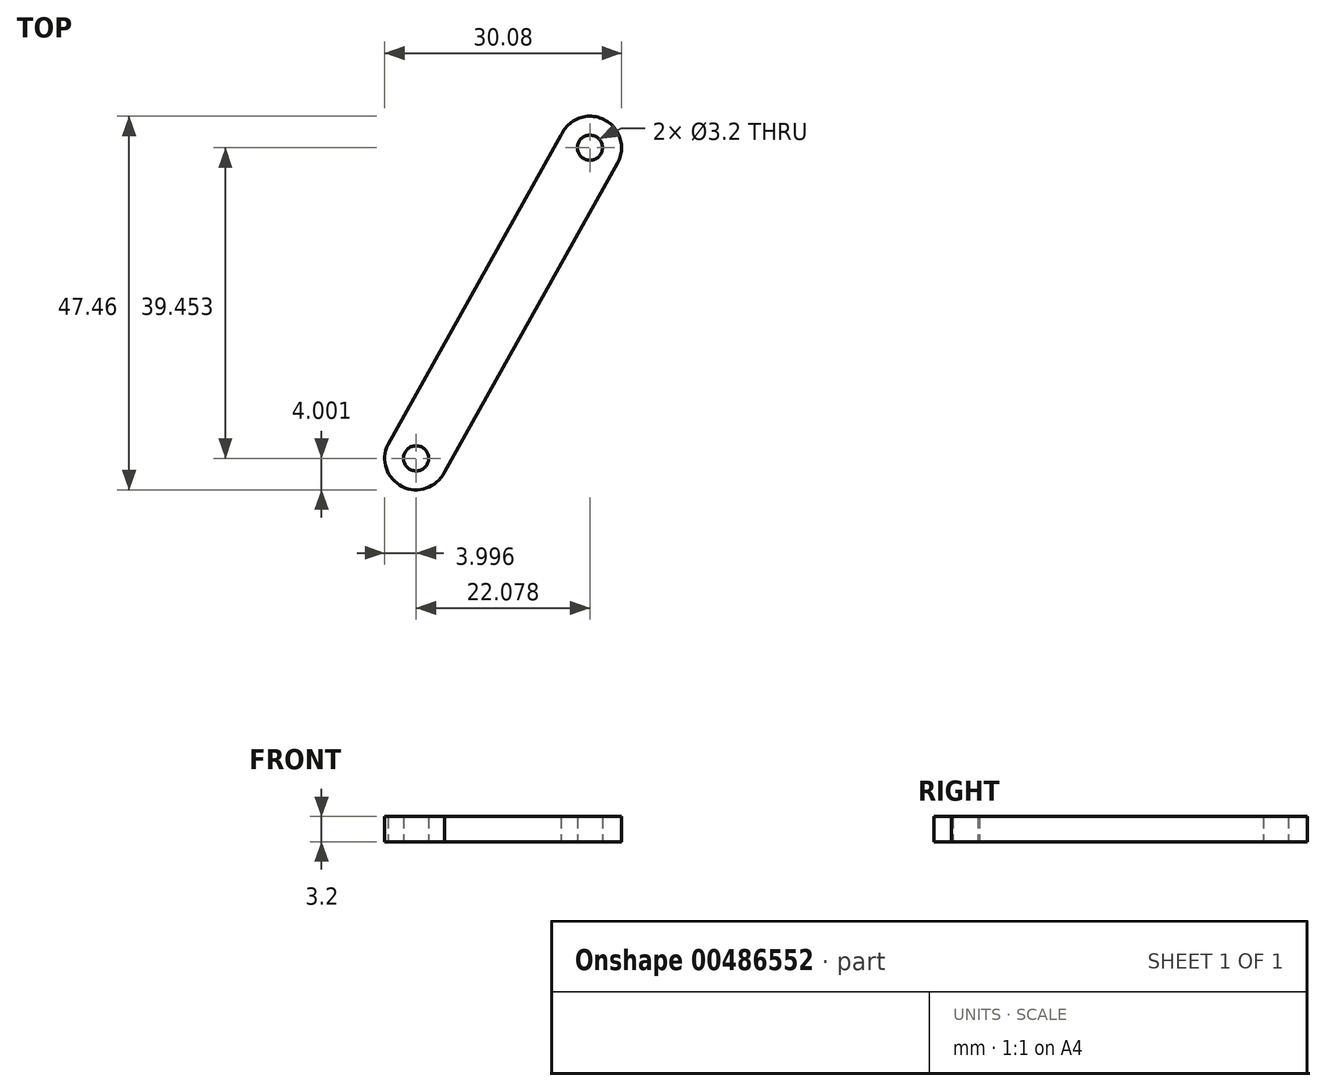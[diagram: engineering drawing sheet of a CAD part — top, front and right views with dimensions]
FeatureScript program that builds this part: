
annotation { "Feature Type Name" : "Feature", "Feature Type Description" : "" }
export const myFeature = defineFeature(function(context is Context, id is Id, definition is map)
    precondition{}
    {
        {
            var Q0;
            Q0=qCreatedBy(makeId("Top.planeOp"),FACE);
            var sketch = newSketch(context, id + "F0", { "sketchPlane" : qUnion([Q0])});
            skLineSegment(sketch, "E0", {"start": v(-21.3, -14.77) * mm, "end": v(-43.28, -54.04) * mm});
            skLineSegment(sketch, "E1", {"start": v(-50.45, -50.5) * mm, "end": v(-28.47, -11.24) * mm});
            skArc(sketch, "E2", {"start": v(-21.3, -14.77) * mm, "mid": v(-23.02, -9.22) * mm, "end": v(-28.47, -11.24) * mm});
            skArc(sketch, "E3", {"start": v(-50.45, -50.5) * mm, "mid": v(-48.63, -55.86) * mm, "end": v(-43.28, -54.04) * mm});
            skCircle(sketch, "E4", {"center": v(-24.79, -12.82) * mm, "radius": 1.6 * mm});
            skCircle(sketch, "E5", {"center": v(-46.86, -52.27) * mm, "radius": 1.6 * mm});
            skSolve(sketch);
        }
        {
            var Q0;
            Q0=makeQuery(id+"F0.imprint","IMPRINT",FACE,{"disambiguationData":[TD([[makeQuery(id+"F0.imprint","IMPRINT",EDGE,{"derivedFrom":sQuery(id+"F0.wireOp",EDGE,"E0")}),-1.0]])]});
            extrude(context, id + "F1", {"entities" : qUnion([Q0]), "depth" : 3.2 * mm, "offsetDistance" : 25 * mm});
        }
    });
